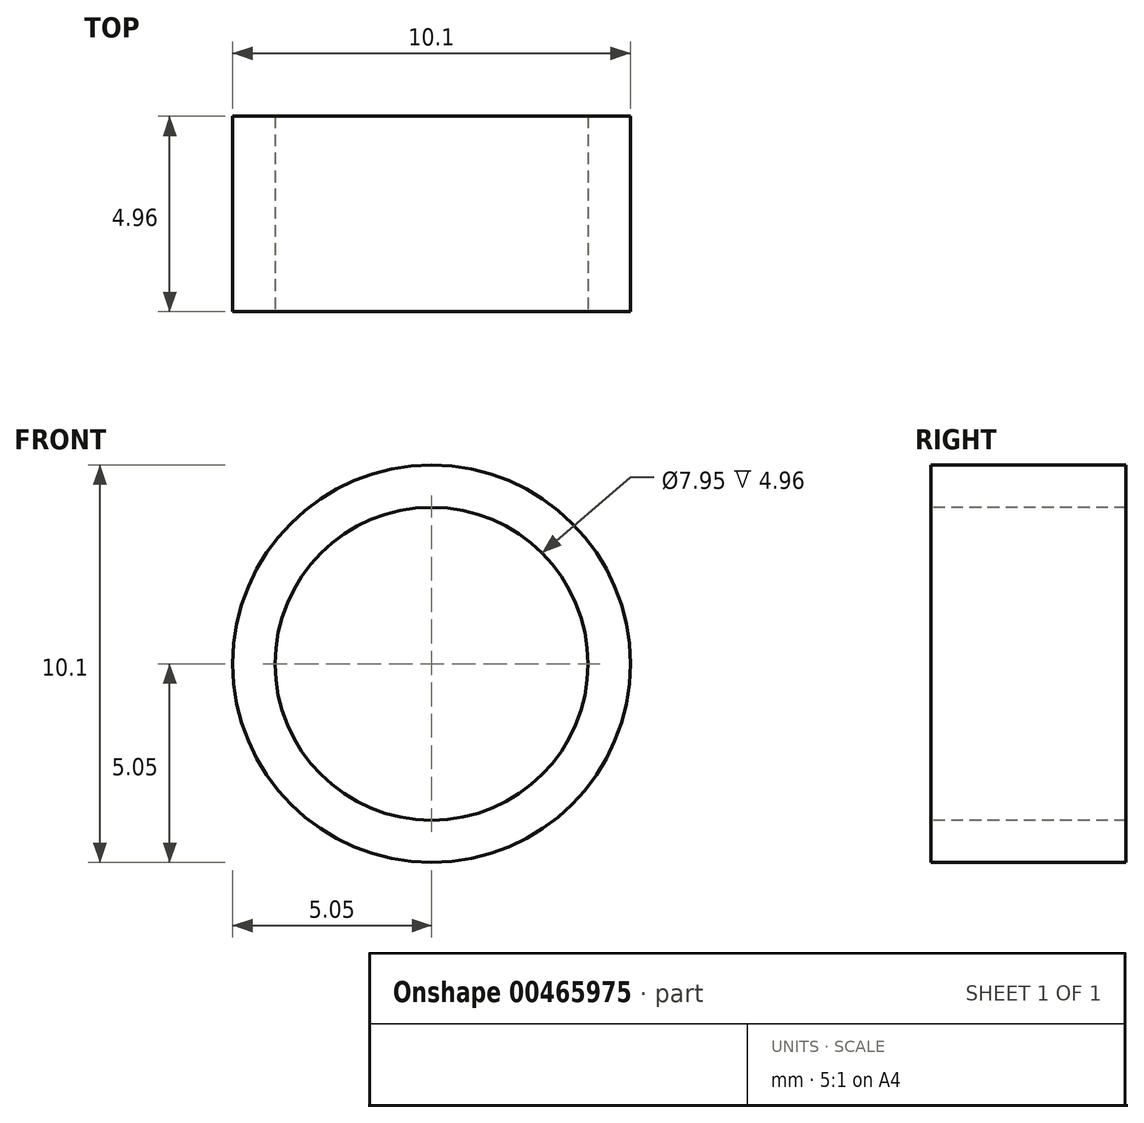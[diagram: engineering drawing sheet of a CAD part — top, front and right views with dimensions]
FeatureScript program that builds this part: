
annotation { "Feature Type Name" : "Feature", "Feature Type Description" : "" }
export const myFeature = defineFeature(function(context is Context, id is Id, definition is map)
    precondition{}
    {
        {
            var Q0;
            Q0=qCreatedBy(makeId("Right.planeOp"),FACE);
            var sketch = newSketch(context, id + "F0", { "sketchPlane" : qUnion([Q0])});
            skLineSegment(sketch, "E0.bottom", {"start": v(2.48, 3.98) * mm, "end": v(-2.48, 3.98) * mm});
            skLineSegment(sketch, "E0.top", {"start": v(2.48, 5.05) * mm, "end": v(-2.48, 5.05) * mm});
            skLineSegment(sketch, "E0.left", {"start": v(2.48, 3.98) * mm, "end": v(2.48, 5.05) * mm});
            skLineSegment(sketch, "E0.right", {"start": v(-2.48, 3.98) * mm, "end": v(-2.48, 5.05) * mm});
            skPoint(sketch, "E0.middle", {"position": v(0, 4.51) * mm});
            skLineSegment(sketch, "E1", {"start": v(-3.4, 0) * mm, "end": v(3.9, 0) * mm, "construction": true});
            skSolve(sketch);
        }
        {
            var Q0;
            Q0=makeQuery(id+"F0.imprint","IMPRINT",FACE,{"disambiguationData":[TD([[makeQuery(id+"F0.imprint","IMPRINT",EDGE,{"derivedFrom":sQuery(id+"F0.wireOp",EDGE,"E0.bottom")}),-1.0]])]});
            var Q1;
            Q1=sQuery(id+"F0.wireOp",EDGE,"E1");
            revolve(context, id + "F1", {"entities" : qUnion([Q0]), "axis" : qUnion([Q1]), "revolveType" : RevolveType.FULL});
        }
    });
